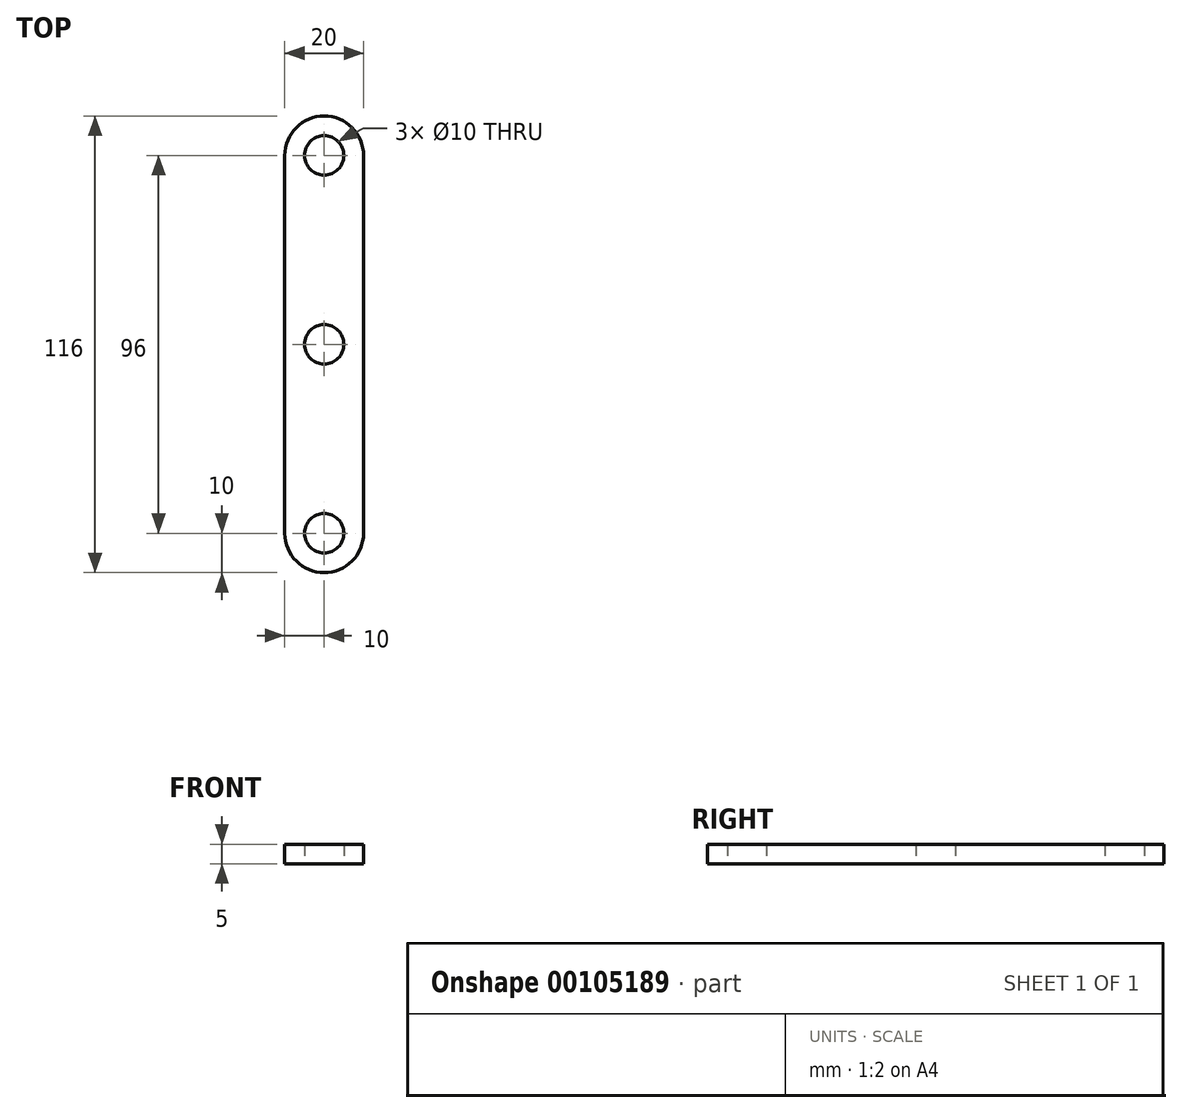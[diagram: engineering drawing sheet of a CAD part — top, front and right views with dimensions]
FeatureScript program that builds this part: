
annotation { "Feature Type Name" : "Feature", "Feature Type Description" : "" }
export const myFeature = defineFeature(function(context is Context, id is Id, definition is map)
    precondition{}
    {
        {
            var Q0;
            Q0=qCreatedBy(makeId("Top.planeOp"),FACE);
            var sketch = newSketch(context, id + "F0", { "sketchPlane" : qUnion([Q0])});
            skCircle(sketch, "E0", {"center": v(0, 0) * mm, "radius": 5 * mm});
            skCircle(sketch, "E1", {"center": v(0, 48) * mm, "radius": 5 * mm});
            skArc(sketch, "E2.0", {"start": v(-10, 0) * mm, "mid": v(0, -10) * mm, "end": v(10, 0) * mm});
            skArc(sketch, "E3", {"start": v(10, 96) * mm, "mid": v(0, 106) * mm, "end": v(-10, 96) * mm});
            skCircle(sketch, "E4", {"center": v(0, 96) * mm, "radius": 5 * mm});
            skLineSegment(sketch, "E5", {"start": v(-10, 96) * mm, "end": v(-10, 0) * mm});
            skLineSegment(sketch, "E6", {"start": v(10, 96) * mm, "end": v(10, 0) * mm});
            skSolve(sketch);
        }
        {
            var Q0;
            Q0=makeQuery(id+"F0.imprint","IMPRINT",FACE,{"disambiguationData":[TD([[makeQuery(id+"F0.imprint","IMPRINT",EDGE,{"derivedFrom":sQuery(id+"F0.wireOp",EDGE,"E0")}),-1.0]])]});
            extrude(context, id + "F1", {"entities" : qUnion([Q0]), "depth" : 5 * mm});
        }
    });
